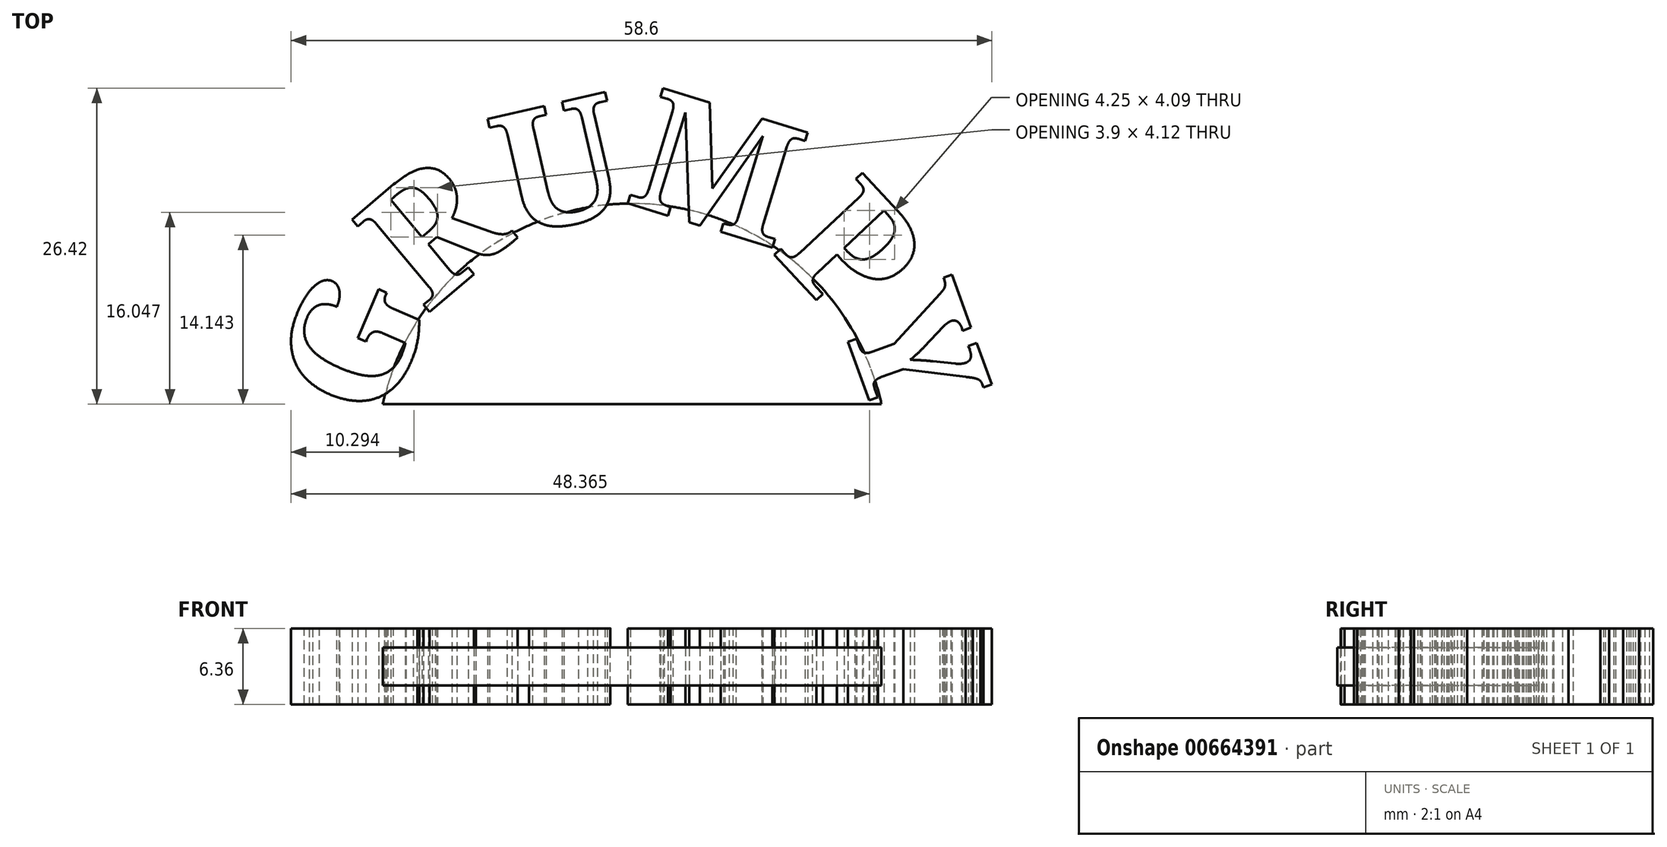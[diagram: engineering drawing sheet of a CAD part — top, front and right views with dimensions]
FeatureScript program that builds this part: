
annotation { "Feature Type Name" : "Feature", "Feature Type Description" : "" }
export const myFeature = defineFeature(function(context is Context, id is Id, definition is map)
    precondition{}
    {
        {
            var Q0;
            Q0=qCreatedBy(makeId("Top.planeOp"),FACE);
            var sketch = newSketch(context, id + "F0", { "sketchPlane" : qUnion([Q0])});
            skArc(sketch, "E0", {"start": v(20.96, 0) * mm, "mid": v(0, 20.96) * mm, "end": v(-20.96, 0) * mm, "construction": true});
            skLineSegment(sketch, "E1", {"start": v(20.96, 0) * mm, "end": v(-20.96, 0) * mm, "construction": true});
            skText(sketch, "E2", { "text": "G", "fontName": "NotoSerif-Bold.ttf"});
            skText(sketch, "E3", { "text": "R", "fontName": "NotoSerif-Bold.ttf"});
            skText(sketch, "E4", { "text": "U", "fontName": "NotoSerif-Bold.ttf"});
            skText(sketch, "E5", { "text": "M", "fontName": "NotoSerif-Bold.ttf"});
            skText(sketch, "E6", { "text": "P", "fontName": "NotoSerif-Bold.ttf"});
            skText(sketch, "E7", { "text": "Y", "fontName": "NotoSerif-Bold.ttf"});
            skLineSegment(sketch, "E8", {"start": v(0, 0) * mm, "end": v(-18.7, 7.94) * mm, "construction": true});
            skLineSegment(sketch, "E9", {"start": v(0, 0) * mm, "end": v(-13.06, 15.57) * mm, "construction": true});
            skLineSegment(sketch, "E10", {"start": v(0, 0) * mm, "end": v(-4.57, 19.8) * mm, "construction": true});
            skLineSegment(sketch, "E11", {"start": v(0, 0) * mm, "end": v(5.94, 19.43) * mm, "construction": true});
            skLineSegment(sketch, "E12", {"start": v(0, 0) * mm, "end": v(14.86, 13.86) * mm, "construction": true});
            skLineSegment(sketch, "E13", {"start": v(0, 0) * mm, "end": v(19.1, 6.95) * mm, "construction": true});
            const initialGuessF0  = {"E2": [-0.02093, 0.0027, 0.39073, 0.9205, 0.01016], "E3": [-0.01725, 0.01205, 0.76604, 0.64279, 0.01016], "E4": [-0.01004, 0.01854, 0.97437, 0.22495, 0.01016], "E5": [-0.00073, 0.02147, 0.9563, -0.29237, 0.01016], "E6": [0.01162, 0.01733, 0.682, -0.73135, 0.01016], "E7": [0.01727, 0.01197, 0.34202, -0.9397, 0.01016]};
            skSetInitialGuess(sketch, initialGuessF0);
            skSolve(sketch);
        }
        {
            var Q0;
            Q0 = qSketchRegion(id + "F0", true);
            extrude(context, id + "F1", {"entities" : qUnion([Q0]), "depth" : 3.17 * mm, "offsetDistance" : 25.4 * mm, "hasSecondDirection" : true, "secondDirectionOppositeDirection" : true, "secondDirectionDepth" : 3.17 * mm});
        }
        {
            var Q0;
            Q0=qCreatedBy(makeId("Top.planeOp"),FACE);
            var sketch = newSketch(context, id + "F2", { "sketchPlane" : qUnion([Q0])});
            skArc(sketch, "E14", {"start": v(20.85, 4.57) * mm, "mid": v(0, 21.35) * mm, "end": v(-20.85, 4.57) * mm});
            skLineSegment(sketch, "E15", {"start": v(20.85, 4.57) * mm, "end": v(-20.85, 4.57) * mm});
            skLineSegment(sketch, "E16", {"start": v(0, 0) * mm, "end": v(-6.33, 0) * mm, "construction": true});
            skSolve(sketch);
        }
        {
            var Q0;
            Q0=makeQuery(id+"F2.imprint","IMPRINT",FACE,{"disambiguationData":[TD([[makeQuery(id+"F2.imprint","IMPRINT",EDGE,{"derivedFrom":sQuery(id+"F2.wireOp",EDGE,"E14")}),1.0]])]});
            extrude(context, id + "F3", {"entities" : qUnion([Q0]), "depth" : 1.59 * mm, "offsetDistance" : 25.4 * mm, "hasSecondDirection" : true, "secondDirectionOppositeDirection" : true, "secondDirectionDepth" : 1.59 * mm});
        }
    });
